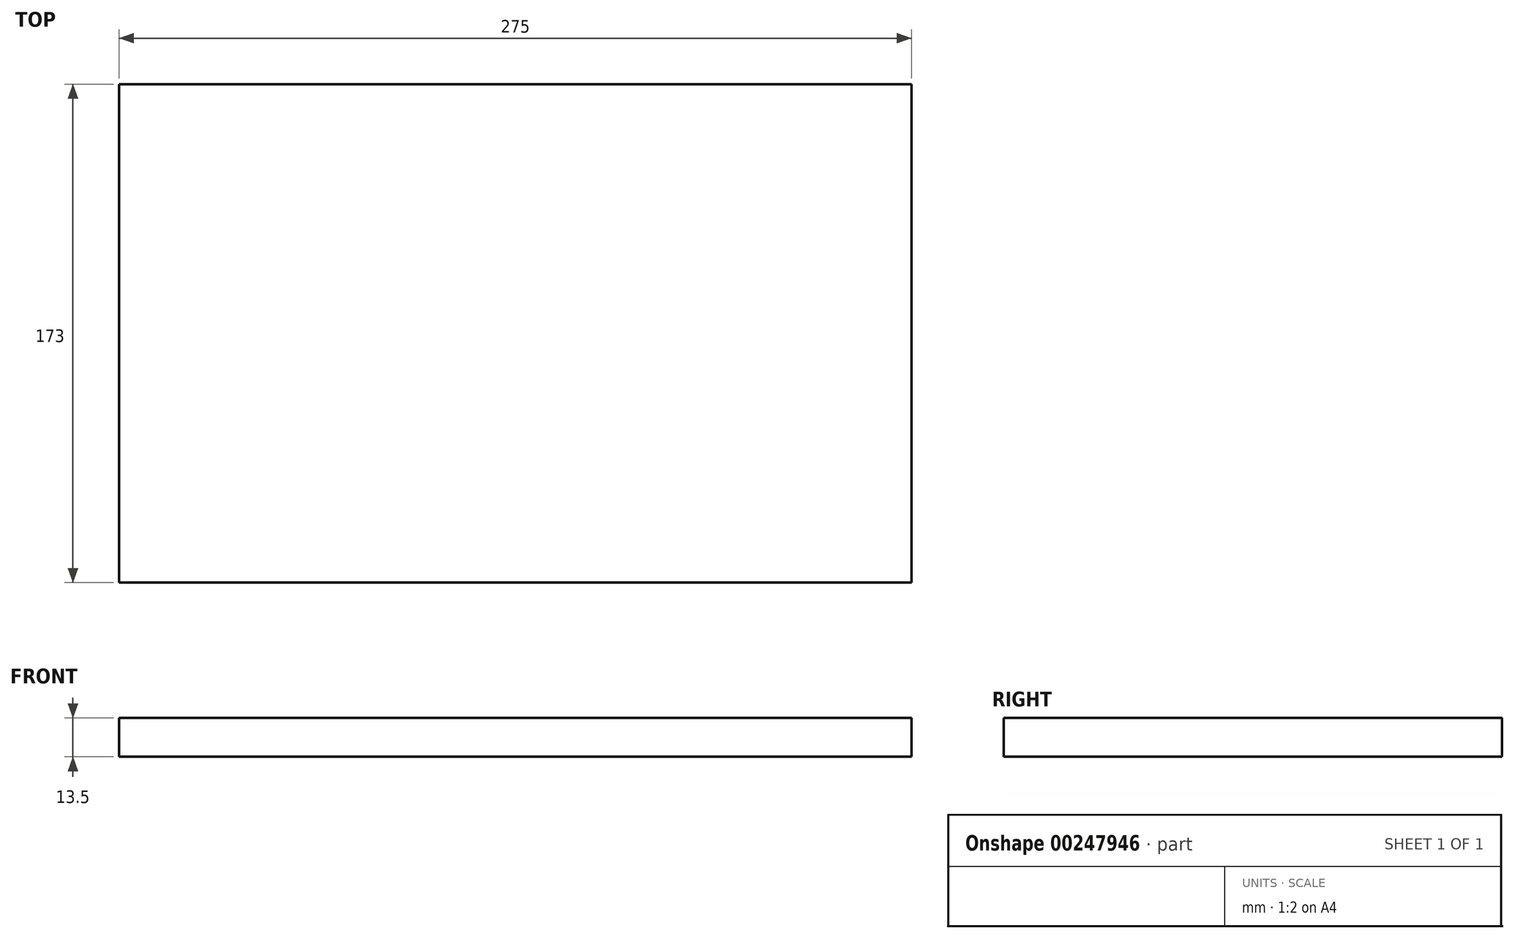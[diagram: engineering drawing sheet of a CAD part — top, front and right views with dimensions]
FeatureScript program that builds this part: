
annotation { "Feature Type Name" : "Feature", "Feature Type Description" : "" }
export const myFeature = defineFeature(function(context is Context, id is Id, definition is map)
    precondition{}
    {
        {
            var Q0;
            Q0=qCreatedBy(makeId("Top.planeOp"),FACE);
            var sketch = newSketch(context, id + "F0", { "sketchPlane" : qUnion([Q0])});
            skLineSegment(sketch, "E0.bottom", {"start": v(-139.53, 101.37) * mm, "end": v(135.47, 101.37) * mm});
            skLineSegment(sketch, "E0.top", {"start": v(-139.53, -71.63) * mm, "end": v(135.47, -71.63) * mm});
            skLineSegment(sketch, "E0.left", {"start": v(-139.53, 101.37) * mm, "end": v(-139.53, -71.63) * mm});
            skLineSegment(sketch, "E0.right", {"start": v(135.47, 101.37) * mm, "end": v(135.47, -71.63) * mm});
            skSolve(sketch);
        }
        {
            var Q0;
            Q0=makeQuery(id+"F0.imprint","IMPRINT",FACE,{"disambiguationData":[TD([[makeQuery(id+"F0.imprint","IMPRINT",EDGE,{"derivedFrom":sQuery(id+"F0.wireOp",EDGE,"E0.bottom")}),-1.0]])]});
            extrude(context, id + "F1", {"entities" : qUnion([Q0]), "depth" : 13.5 * mm});
        }
    });
